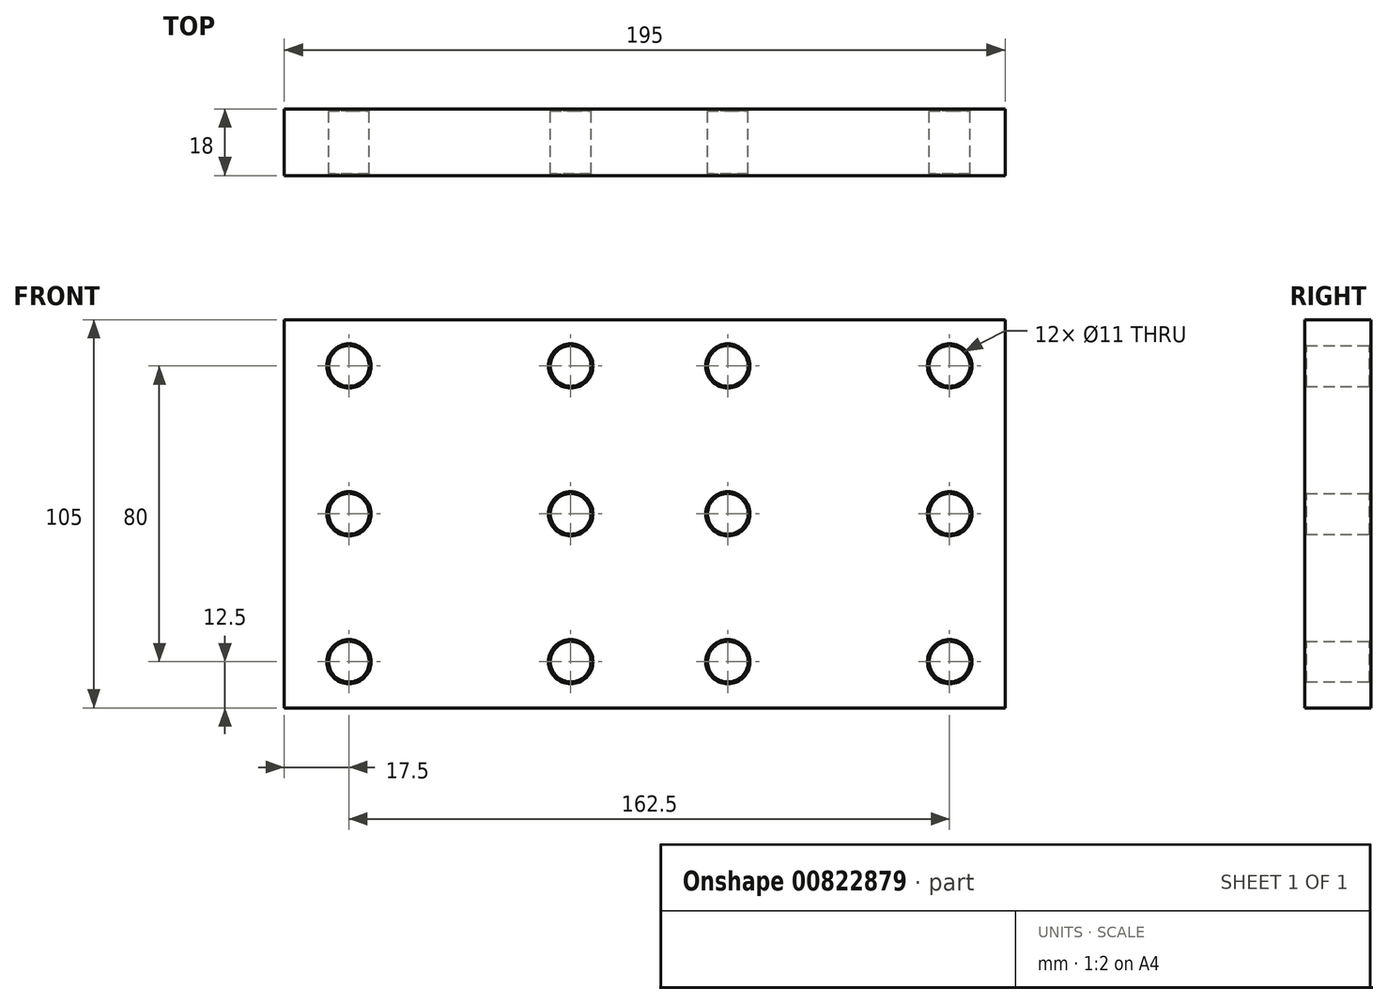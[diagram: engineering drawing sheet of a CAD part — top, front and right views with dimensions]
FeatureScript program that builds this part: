
annotation { "Feature Type Name" : "Feature", "Feature Type Description" : "" }
export const myFeature = defineFeature(function(context is Context, id is Id, definition is map)
    precondition{}
    {
        {
            var Q0;
            Q0=qCreatedBy(makeId("Front.planeOp"),FACE);
            var sketch = newSketch(context, id + "F0", { "sketchPlane" : qUnion([Q0])});
            skLineSegment(sketch, "E0.bottom", {"start": v(-97.5, -52.5) * mm, "end": v(97.5, -52.5) * mm});
            skLineSegment(sketch, "E0.top", {"start": v(-97.5, 52.5) * mm, "end": v(97.5, 52.5) * mm});
            skLineSegment(sketch, "E0.left", {"start": v(-97.5, -52.5) * mm, "end": v(-97.5, 52.5) * mm});
            skLineSegment(sketch, "E0.right", {"start": v(97.5, -52.5) * mm, "end": v(97.5, 52.5) * mm});
            skPoint(sketch, "E0.middle", {"position": v(0, 0) * mm});
            skLineSegment(sketch, "E1", {"start": v(-50, 0) * mm, "end": v(0, 0) * mm, "construction": true});
            skLineSegment(sketch, "E2", {"start": v(0, 0) * mm, "end": v(52.5, 0) * mm, "construction": true});
            skLineSegment(sketch, "E3.bottom", {"start": v(-20, 40) * mm, "end": v(-80, 40) * mm, "construction": true});
            skLineSegment(sketch, "E3.top", {"start": v(-20, -40) * mm, "end": v(-80, -40) * mm, "construction": true});
            skLineSegment(sketch, "E3.left", {"start": v(-20, 40) * mm, "end": v(-20, -40) * mm, "construction": true});
            skLineSegment(sketch, "E3.right", {"start": v(-80, 40) * mm, "end": v(-80, -40) * mm, "construction": true});
            skPoint(sketch, "E3.middle", {"position": v(-50, 0) * mm});
            skLineSegment(sketch, "E4.bottom", {"start": v(22.5, 40) * mm, "end": v(82.5, 40) * mm, "construction": true});
            skLineSegment(sketch, "E4.top", {"start": v(22.5, -40) * mm, "end": v(82.5, -40) * mm, "construction": true});
            skLineSegment(sketch, "E4.left", {"start": v(22.5, 40) * mm, "end": v(22.5, -40) * mm, "construction": true});
            skLineSegment(sketch, "E4.right", {"start": v(82.5, 40) * mm, "end": v(82.5, -40) * mm, "construction": true});
            skPoint(sketch, "E4.middle", {"position": v(52.5, 0) * mm});
            skLineSegment(sketch, "E5", {"start": v(-80, 0) * mm, "end": v(-20, 0) * mm, "construction": true});
            skLineSegment(sketch, "E6", {"start": v(82.5, 0) * mm, "end": v(22.5, 0) * mm, "construction": true});
            skCircle(sketch, "E7", {"center": v(-80, 40) * mm, "radius": 5.5 * mm});
            skCircle(sketch, "E8", {"center": v(22.5, 40) * mm, "radius": 5.5 * mm});
            skCircle(sketch, "E9.0.1.0", {"center": v(-80, 0) * mm, "radius": 5.5 * mm});
            skCircle(sketch, "E9.0.1.1", {"center": v(22.5, 0) * mm, "radius": 5.5 * mm});
            skCircle(sketch, "E9.0.2.0", {"center": v(-80, -40) * mm, "radius": 5.5 * mm});
            skCircle(sketch, "E9.0.2.1", {"center": v(22.5, -40) * mm, "radius": 5.5 * mm});
            skCircle(sketch, "E9.1.0.0", {"center": v(-20, 40) * mm, "radius": 5.5 * mm});
            skCircle(sketch, "E9.1.0.1", {"center": v(82.5, 40) * mm, "radius": 5.5 * mm});
            skCircle(sketch, "E9.1.1.0", {"center": v(-20, 0) * mm, "radius": 5.5 * mm});
            skCircle(sketch, "E9.1.1.1", {"center": v(82.5, 0) * mm, "radius": 5.5 * mm});
            skCircle(sketch, "E9.1.2.0", {"center": v(-20, -40) * mm, "radius": 5.5 * mm});
            skCircle(sketch, "E9.1.2.1", {"center": v(82.5, -40) * mm, "radius": 5.5 * mm});
            skLineSegment(sketch, "E9.direction1", {"start": v(-80, 40) * mm, "end": v(-20, 40) * mm, "construction": true});
            skLineSegment(sketch, "E9.direction2", {"start": v(-80, 40) * mm, "end": v(-80, 0) * mm, "construction": true});
            skSolve(sketch);
        }
        {
            var Q0;
            Q0 = qSketchRegion(id + "F0", true);
            extrude(context, id + "F1", {"entities" : qUnion([Q0]), "depth" : 18 * mm, "offsetDistance" : 25 * mm});
        }
        {
            var Q0;
            Q0=makeQuery(id+"F1.opExtrude","SWEPT_FACE",FACE,{"disambiguationData":[OSD([sQuery(id+"F0.wireOp",EDGE,"E7")])]});
            var Q1;
            Q1=makeQuery(id+"F1.opExtrude","SWEPT_FACE",FACE,{"disambiguationData":[OSD([sQuery(id+"F0.wireOp",EDGE,"E9.0.1.0")])]});
            var Q2;
            Q2=makeQuery(id+"F1.opExtrude","SWEPT_FACE",FACE,{"disambiguationData":[OSD([sQuery(id+"F0.wireOp",EDGE,"E9.0.2.0")])]});
            var Q3;
            Q3=makeQuery(id+"F1.opExtrude","SWEPT_FACE",FACE,{"disambiguationData":[OSD([sQuery(id+"F0.wireOp",EDGE,"E9.1.0.0")])]});
            var Q4;
            Q4=makeQuery(id+"F1.opExtrude","SWEPT_FACE",FACE,{"disambiguationData":[OSD([sQuery(id+"F0.wireOp",EDGE,"E9.1.1.0")])]});
            var Q5;
            Q5=makeQuery(id+"F1.opExtrude","SWEPT_FACE",FACE,{"disambiguationData":[OSD([sQuery(id+"F0.wireOp",EDGE,"E9.1.2.0")])]});
            var Q6;
            Q6=makeQuery(id+"F1.opExtrude","SWEPT_FACE",FACE,{"disambiguationData":[OSD([sQuery(id+"F0.wireOp",EDGE,"E8")])]});
            var Q7;
            Q7=makeQuery(id+"F1.opExtrude","SWEPT_FACE",FACE,{"disambiguationData":[OSD([sQuery(id+"F0.wireOp",EDGE,"E9.0.1.1")])]});
            var Q8;
            Q8=makeQuery(id+"F1.opExtrude","SWEPT_FACE",FACE,{"disambiguationData":[OSD([sQuery(id+"F0.wireOp",EDGE,"E9.0.2.1")])]});
            var Q9;
            Q9=makeQuery(id+"F1.opExtrude","SWEPT_FACE",FACE,{"disambiguationData":[OSD([sQuery(id+"F0.wireOp",EDGE,"E9.1.0.1")])]});
            var Q10;
            Q10=makeQuery(id+"F1.opExtrude","SWEPT_FACE",FACE,{"disambiguationData":[OSD([sQuery(id+"F0.wireOp",EDGE,"E9.1.1.1")])]});
            var Q11;
            Q11=makeQuery(id+"F1.opExtrude","SWEPT_FACE",FACE,{"disambiguationData":[OSD([sQuery(id+"F0.wireOp",EDGE,"E9.1.2.1")])]});
            chamfer(context, id + "F2", {"entities" : qUnion([Q0, Q1, Q2, Q3, Q4, Q5, Q6, Q7, Q8, Q9, Q10, Q11]), "width" : 0.5 * mm, "tangentPropagation" : true});
        }
    });
